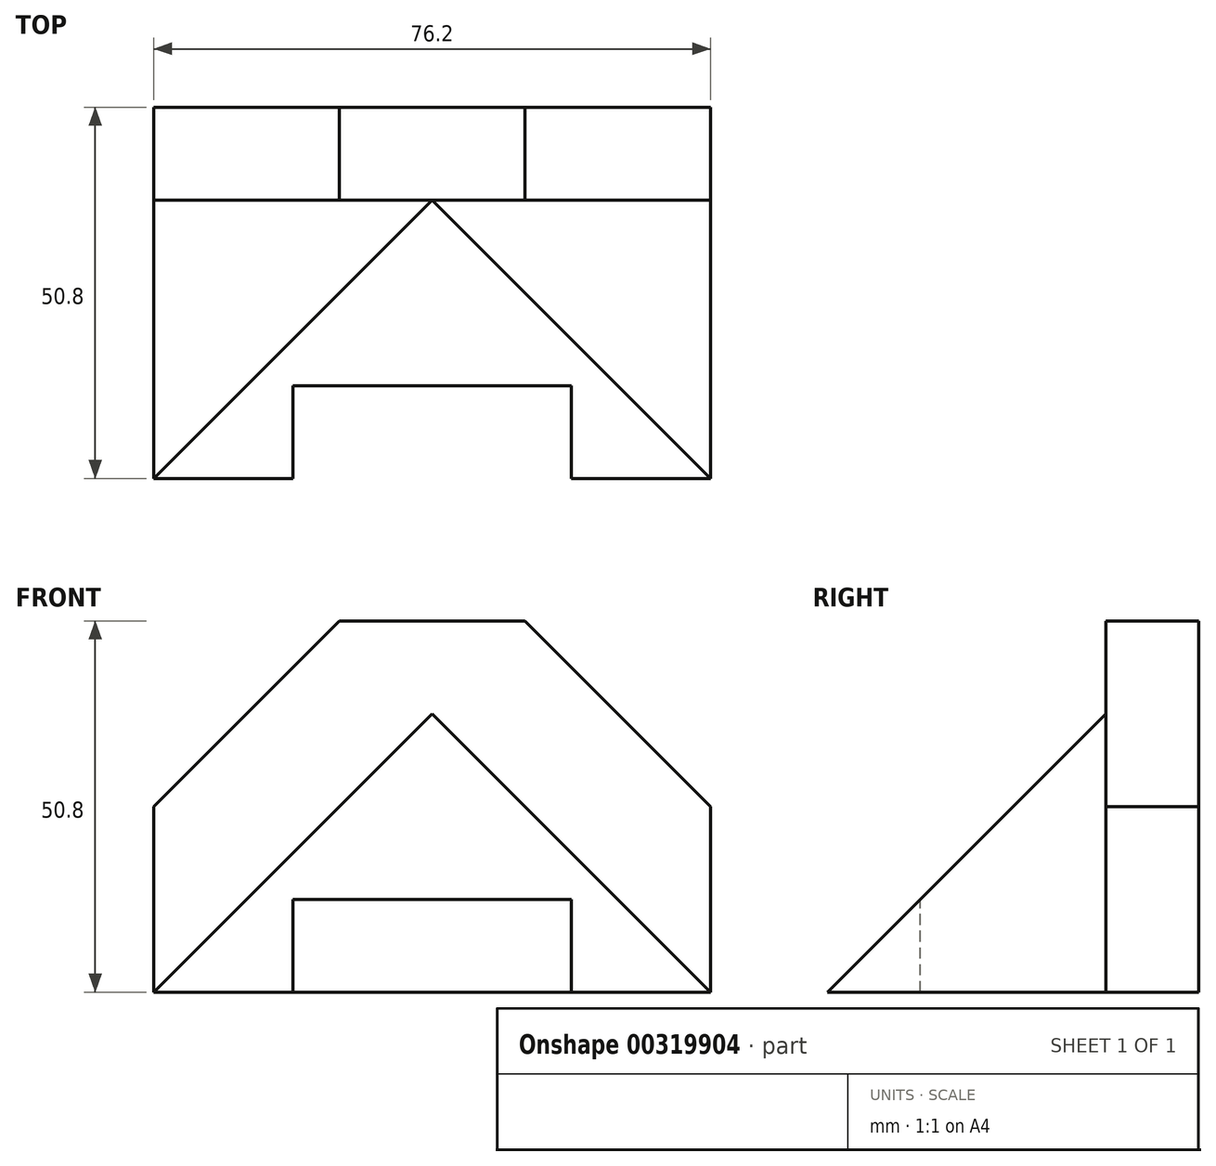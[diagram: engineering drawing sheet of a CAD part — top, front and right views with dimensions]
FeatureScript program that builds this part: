
annotation { "Feature Type Name" : "Feature", "Feature Type Description" : "" }
export const myFeature = defineFeature(function(context is Context, id is Id, definition is map)
    precondition{}
    {
        {
            var Q0;
            Q0=qCreatedBy(makeId("Right.planeOp"),FACE);
            var sketch = newSketch(context, id + "F0", { "sketchPlane" : qUnion([Q0])});
            skLineSegment(sketch, "E0", {"start": v(0, 0) * mm, "end": v(-50.8, 0) * mm});
            skLineSegment(sketch, "E1", {"start": v(0, 0) * mm, "end": v(0, 50.8) * mm});
            skLineSegment(sketch, "E2", {"start": v(0, 50.8) * mm, "end": v(-12.7, 50.8) * mm});
            skLineSegment(sketch, "E3", {"start": v(-12.7, 50.8) * mm, "end": v(-12.7, 0) * mm});
            skLineSegment(sketch, "E4", {"start": v(-12.7, 0) * mm, "end": v(-12.7, 38.1) * mm});
            skLineSegment(sketch, "E5", {"start": v(-12.7, 38.1) * mm, "end": v(-50.8, 0) * mm});
            skSolve(sketch);
        }
        {
            var Q0;
            Q0 = qSketchRegion(id + "F0", true);
            extrude(context, id + "F1", {"entities" : qUnion([Q0]), "endBound" : BoundingType.SYMMETRIC, "depth" : 76.2 * mm});
        }
        {
            var Q0;
            Q0=makeQuery(id+"F1.opExtrude","SWEPT_FACE",FACE,{"disambiguationData":[OSD([sQuery(id+"F0.wireOp",EDGE,"E1")])]});
            var sketch = newSketch(context, id + "F2", { "sketchPlane" : qUnion([Q0])});
            skLineSegment(sketch, "E6", {"start": v(-38.1, 0) * mm, "end": v(-38.1, 25.4) * mm});
            skLineSegment(sketch, "E7", {"start": v(38.1, 0) * mm, "end": v(38.1, 25.4) * mm});
            skLineSegment(sketch, "E8", {"start": v(0, 0) * mm, "end": v(0, 38.1) * mm, "construction": true});
            skLineSegment(sketch, "E9", {"start": v(0, 38.1) * mm, "end": v(0, 50.8) * mm, "construction": true});
            skLineSegment(sketch, "E10", {"start": v(-12.7, 50.8) * mm, "end": v(12.7, 50.8) * mm});
            skLineSegment(sketch, "E11", {"start": v(-38.1, 25.4) * mm, "end": v(-12.7, 50.8) * mm});
            skLineSegment(sketch, "E12", {"start": v(12.7, 50.8) * mm, "end": v(38.1, 25.4) * mm});
            skLineSegment(sketch, "E13", {"start": v(-38.1, 0) * mm, "end": v(0, 38.1) * mm});
            skLineSegment(sketch, "E14", {"start": v(0, 38.1) * mm, "end": v(38.1, 0) * mm});
            skLineSegment(sketch, "E15", {"start": v(-38.1, 0) * mm, "end": v(-19.05, 0) * mm});
            skLineSegment(sketch, "E16", {"start": v(-19.05, 0) * mm, "end": v(-19.05, 12.7) * mm});
            skLineSegment(sketch, "E17", {"start": v(38.1, 0) * mm, "end": v(19.05, 0) * mm});
            skLineSegment(sketch, "E18", {"start": v(19.05, 0) * mm, "end": v(19.05, 12.7) * mm});
            skLineSegment(sketch, "E19", {"start": v(-19.05, 12.7) * mm, "end": v(19.05, 12.7) * mm});
            skLineSegment(sketch, "E20", {"start": v(12.7, 50.8) * mm, "end": v(38.1, 50.8) * mm});
            skLineSegment(sketch, "E21", {"start": v(38.1, 50.8) * mm, "end": v(38.1, 25.4) * mm});
            skLineSegment(sketch, "E22", {"start": v(-12.7, 50.8) * mm, "end": v(-38.1, 50.8) * mm});
            skLineSegment(sketch, "E23", {"start": v(-38.1, 50.8) * mm, "end": v(-38.1, 25.4) * mm});
            skSolve(sketch);
        }
        {
            var Q0;
            Q0=makeQuery(id+"F2.imprint","IMPRINT",FACE,{"disambiguationData":[TD([[makeQuery(id+"F2.imprint","IMPRINT",EDGE,{"derivedFrom":sQuery(id+"F2.wireOp",EDGE,"E6")}),-1.0]])]});
            var Q1;
            Q1=makeQuery(id+"F2.imprint","IMPRINT",FACE,{"disambiguationData":[TD([[makeQuery(id+"F2.imprint","IMPRINT",EDGE,{"derivedFrom":sQuery(id+"F2.wireOp",EDGE,"E12")}),1.0]])]});
            var Q2;
            Q2=makeQuery(id+"F2.imprint","IMPRINT",FACE,{"disambiguationData":[TD([[makeQuery(id+"F2.imprint","IMPRINT",EDGE,{"derivedFrom":sQuery(id+"F2.wireOp",EDGE,"E11")}),1.0]])]});
            extrude(context, id + "F3", {"entities" : qUnion([Q0, Q1, Q2]), "operationType" : NewBodyOperationType.REMOVE, "endBound" : BoundingType.THROUGH_ALL, "oppositeDirection" : true, "depth" : 25.4 * mm});
        }
        {
            var Q0;
            Q0=makeQuery(id+"F2.imprint","IMPRINT",FACE,{"disambiguationData":[TD([[makeQuery(id+"F2.imprint","IMPRINT",EDGE,{"derivedFrom":sQuery(id+"F2.wireOp",EDGE,"E6")}),-1.0]])]});
            extrude(context, id + "F4", {"entities" : qUnion([Q0]), "operationType" : NewBodyOperationType.ADD, "oppositeDirection" : true, "depth" : 12.7 * mm});
        }
        {
            var Q0;
            Q0=qCreatedBy(makeId("Right.planeOp"),FACE);
            var sketch = newSketch(context, id + "F5", { "sketchPlane" : qUnion([Q0])});
            skLineSegment(sketch, "E24", {"start": v(-50.8, 0) * mm, "end": v(-38.1, 0) * mm});
            skLineSegment(sketch, "E25", {"start": v(-38.1, 0) * mm, "end": v(-38.1, 12.7) * mm});
            skLineSegment(sketch, "E26", {"start": v(-50.8, 0) * mm, "end": v(-38.1, 12.7) * mm});
            skSolve(sketch);
        }
        {
            var Q0;
            Q0 = qSketchRegion(id + "F5", true);
            extrude(context, id + "F6", {"entities" : qUnion([Q0]), "operationType" : NewBodyOperationType.REMOVE, "endBound" : BoundingType.SYMMETRIC, "oppositeDirection" : true, "depth" : 38.1 * mm});
        }
    });
